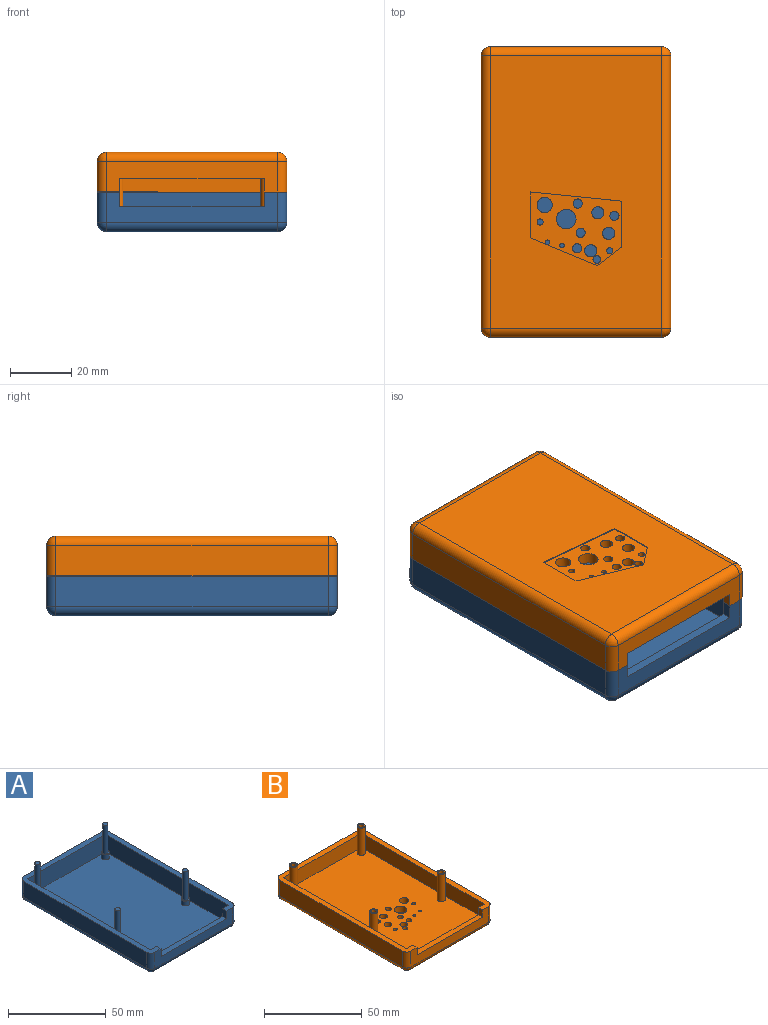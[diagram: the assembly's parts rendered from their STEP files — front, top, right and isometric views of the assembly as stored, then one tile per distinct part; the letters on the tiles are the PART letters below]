
ASSEMBLY  parts=2 mates=1
PART A: 42 faces, bbox 62x95x23 mm
  f0: plane 56x11mm, normal (0,1,0), area 391.6mm2, adj f2,f3,f4,f9,f39,f40,f41
  f1: plane 56x10mm, normal (0,-1,0), area 335.6mm2, adj f2,f32,f36,f38,f39,f40,f41
  f2: plane 95x62mm, normal (0,0,1), area 756.7mm2, adj f0,f1,f3,f6,f7,f8,f9,f10
  f3: plane 89x11mm, normal (1,0,0), area 979mm2, adj f0,f2,f4,f8
  f4: plane 89x56mm, normal (0,0,1), area 4928.6mm2, adj f0,f3,f8,f9,f11,f13,f15,f17
  f5: plane 89x56mm, normal (0,0,-1), area 4984mm2, adj f30,f31,f35,f36
  f6: plane 89x10mm, normal (-1,0,0), area 890mm2, adj f2,f27,f31,f32
  f7: plane 56x10mm, normal (0,1,0), area 560mm2, adj f2,f27,f29,f30
  f8: plane 56x11mm, normal (0,-1,0), area 616mm2, adj f2,f3,f4,f9
  f9: plane 89x11mm, normal (-1,0,0), area 979mm2, adj f0,f2,f4,f8
  f10: plane 89x10mm, normal (1,0,0), area 890mm2, adj f2,f29,f35,f38
  f11: cylinder r=2.1mm len=4.2mm, axis (0,0,-1), area 39.6mm2, adj f4,f12
  f12: plane 4.2x4.2mm, normal (0,0,1), area 7.9mm2, adj f11,f20
  f13: cylinder r=2.1mm len=4.2mm, axis (0,0,-1), area 39.6mm2, adj f4,f14
  f14: plane 4.2x4.2mm, normal (0,0,1), area 7.9mm2, adj f13,f22
  f15: cylinder r=2.1mm len=4.2mm, axis (0,0,-1), area 39.6mm2, adj f4,f16
  f16: plane 4.2x4.2mm, normal (0,0,1), area 7.9mm2, adj f15,f24
  f17: cylinder r=2.1mm len=4.2mm, axis (0,0,-1), area 39.6mm2, adj f4,f18
  f18: plane 4.2x4.2mm, normal (0,0,1), area 7.9mm2, adj f17,f26
  f19: plane 2.75x2.75mm, normal (0,0,1), area 5.9mm2, adj f20
  f20: cylinder r=1.38mm len=18mm, axis (0,0,-1), area 155.5mm2, adj f12,f19
  f21: plane 2.75x2.75mm, normal (0,0,1), area 5.9mm2, adj f22
  f22: cylinder r=1.38mm len=18mm, axis (0,0,-1), area 155.5mm2, adj f14,f21
  f23: plane 2.75x2.75mm, normal (0,0,1), area 5.9mm2, adj f24
  f24: cylinder r=1.38mm len=18mm, axis (0,0,-1), area 155.5mm2, adj f16,f23
  f25: plane 2.75x2.75mm, normal (0,0,1), area 5.9mm2, adj f26
  f26: cylinder r=1.38mm len=18mm, axis (0,0,-1), area 155.5mm2, adj f18,f25
  f27: cylinder r=3mm len=10mm, axis (0,0,-1), area 47.1mm2, adj f2,f6,f7,f28
  f28: sphere r=3mm, area 14.1mm2, adj f27,f30,f31
  f29: cylinder r=3mm len=10mm, axis (0,0,1), area 47.1mm2, adj f2,f7,f10,f33
  f30: cylinder r=3mm len=56mm, axis (-1,0,0), area 263.9mm2, adj f5,f7,f28,f33
  f31: cylinder r=3mm len=89mm, axis (0,-1,0), area 419.4mm2, adj f5,f6,f28,f34
  f32: cylinder r=3mm len=10mm, axis (0,0,1), area 47.1mm2, adj f1,f2,f6,f34
  f33: sphere r=3mm, area 14.1mm2, adj f29,f30,f35
  f34: sphere r=3mm, area 14.1mm2, adj f31,f32,f36
  f35: cylinder r=3mm len=89mm, axis (0,1,0), area 419.4mm2, adj f5,f10,f33,f37
  f36: cylinder r=3mm len=56mm, axis (1,0,0), area 263.9mm2, adj f1,f5,f34,f37
  f37: sphere r=3mm, area 14.1mm2, adj f35,f36,f38
  f38: cylinder r=3mm len=10mm, axis (0,0,-1), area 47.1mm2, adj f1,f2,f10,f37
  f39: plane 4.75x3mm, normal (-1,0,0), area 14.3mm2, adj f0,f1,f2,f41
  f40: plane 4.75x3mm, normal (1,0,0), area 14.3mm2, adj f0,f1,f2,f41
  f41: plane 47.19x3mm, normal (0,0,1), area 141.6mm2, adj f0,f1,f39,f40
PART B: 64 faces, bbox 62x95x21 mm
  f0: plane 95x62mm, normal (0,0,1), area 756.7mm2, adj f32,f33,f34,f35,f36,f37,f38,f39
  f1: cylinder r=2mm len=4mm, axis (0,0,-1), area 46.5mm2, adj f15,f48
  f2: cylinder r=1mm len=3.7mm, axis (0,0,-1), area 23.2mm2, adj f15,f48
  f3: cylinder r=2mm len=4mm, axis (0,0,-1), area 46.5mm2, adj f15,f48
  f4: cylinder r=1.25mm len=3.7mm, axis (0,0,-1), area 29.1mm2, adj f15,f48
  f5: cylinder r=1.5mm len=3.7mm, axis (0,0,-1), area 34.9mm2, adj f15,f48
  f6: cylinder r=0.75mm len=3.7mm, axis (0,0,-1), area 17.4mm2, adj f15,f48
  f7: cylinder r=1.5mm len=3.7mm, axis (0,0,-1), area 34.9mm2, adj f15,f48
  f8: cylinder r=2mm len=4mm, axis (0,0,-1), area 46.5mm2, adj f15,f48
  f9: cylinder r=1.5mm len=3.7mm, axis (0,0,-1), area 34.9mm2, adj f15,f48
  f10: cylinder r=3.19mm len=6.38mm, axis (0,0,-1), area 74.2mm2, adj f15,f48
  f11: cylinder r=0.75mm len=3.7mm, axis (0,0,-1), area 17.4mm2, adj f15,f48
  f12: cylinder r=1mm len=3.7mm, axis (0,0,-1), area 23.2mm2, adj f15,f48
  f13: cylinder r=2.5mm len=5mm, axis (0,0,-1), area 58.1mm2, adj f15,f48
  f14: cylinder r=1.5mm len=3.7mm, axis (0,0,-1), area 34.9mm2, adj f15,f48
  f15: plane 89x56mm, normal (0,0,1), area 4796.2mm2, adj f1,f2,f3,f4,f5,f6,f7,f8
  f16: cylinder r=2.1mm len=17mm, axis (0,0,-1), area 224.3mm2, adj f15,f18
  f17: cylinder r=1.38mm len=17mm, axis (0,0,-1), area 146.9mm2, adj f18,f19
  f18: plane 4.2x4.2mm, normal (0,0,1), area 7.9mm2, adj f16,f17
  f19: plane 2.75x2.75mm, normal (0,0,1), area 5.9mm2, adj f17
  f20: cylinder r=2.1mm len=17mm, axis (0,0,-1), area 224.3mm2, adj f15,f22
  f21: cylinder r=1.38mm len=17mm, axis (0,0,-1), area 146.9mm2, adj f22,f23
  f22: plane 4.2x4.2mm, normal (0,0,1), area 7.9mm2, adj f20,f21
  f23: plane 2.75x2.75mm, normal (0,0,1), area 5.9mm2, adj f21
  f24: cylinder r=1.38mm len=17mm, axis (0,0,-1), area 146.9mm2, adj f26,f27
  f25: cylinder r=2.1mm len=17mm, axis (0,0,-1), area 224.3mm2, adj f15,f26
  f26: plane 4.2x4.2mm, normal (0,0,1), area 7.9mm2, adj f24,f25
  f27: plane 2.75x2.75mm, normal (0,0,1), area 5.9mm2, adj f24
  f28: cylinder r=1.38mm len=17mm, axis (0,0,-1), area 146.9mm2, adj f30,f31
  f29: cylinder r=2.1mm len=17mm, axis (0,0,-1), area 224.3mm2, adj f15,f30
  f30: plane 4.2x4.2mm, normal (0,0,1), area 7.9mm2, adj f28,f29
  f31: plane 2.75x2.75mm, normal (0,0,1), area 5.9mm2, adj f28
  f32: plane 56x9mm, normal (0,-1,0), area 504mm2, adj f0,f15,f33,f35
  f33: plane 89x9mm, normal (1,0,0), area 801mm2, adj f0,f15,f32,f34
  f34: plane 56x9mm, normal (0,1,0), area 291.4mm2, adj f0,f15,f33,f35,f49,f50,f51
  f35: plane 89x9mm, normal (-1,0,0), area 801mm2, adj f0,f15,f32,f34
  f36: plane 56x10mm, normal (0,-1,0), area 347.4mm2, adj f0,f49,f50,f51,f54,f60,f63
  f37: plane 89x10mm, normal (1,0,0), area 890mm2, adj f0,f52,f54,f55
  f38: plane 56x10mm, normal (0,1,0), area 560mm2, adj f0,f52,f56,f57
  f39: plane 89x10mm, normal (-1,0,0), area 890mm2, adj f0,f57,f61,f63
  f40: plane 89x56mm, normal (0,0,-1), area 4430.2mm2, adj f41,f42,f43,f44,f45,f46,f47,f55
  f41: plane 15x0.3mm, normal (1,0,0), area 4.5mm2, adj f40,f42,f47,f48
  f42: plane 30x3mm, normal (0.1,-1,0), area 9mm2, adj f40,f41,f43,f48
  f43: plane 15x0.3mm, normal (-1,0,0), area 4.5mm2, adj f40,f42,f44,f48
  f44: plane 0.3x0.01mm, normal (-0.42,0.91,0), area 0mm2, adj f40,f43,f45,f48
  f45: plane 22.09x9.13mm, normal (-0.38,0.92,0), area 7.2mm2, adj f40,f44,f46,f48
  f46: plane 7.89x6.12mm, normal (0.61,0.79,0), area 3mm2, adj f40,f45,f47,f48
  f47: plane 0.3x0.01mm, normal (0.62,0.78,0), area 0mm2, adj f40,f41,f46,f48
  f48: plane 30x24.13mm, normal (0,0,-1), area 421.5mm2, adj f1,f2,f3,f4,f5,f6,f7,f8
  f49: plane 4.51x3mm, normal (-1,0,0), area 13.5mm2, adj f0,f34,f36,f51
  f50: plane 4.51x3mm, normal (1,0,0), area 13.5mm2, adj f0,f34,f36,f51
  f51: plane 47.19x3mm, normal (0,0,1), area 141.6mm2, adj f34,f36,f49,f50
  f52: cylinder r=3mm len=10mm, axis (0,0,1), area 47.1mm2, adj f0,f37,f38,f53
  f53: sphere r=3mm, area 14.1mm2, adj f52,f55,f56
  f54: cylinder r=3mm len=10mm, axis (0,0,-1), area 47.1mm2, adj f0,f36,f37,f58
  f55: cylinder r=3mm len=89mm, axis (0,1,0), area 419.4mm2, adj f37,f40,f53,f58
  f56: cylinder r=3mm len=56mm, axis (-1,0,0), area 263.9mm2, adj f38,f40,f53,f59
  f57: cylinder r=3mm len=10mm, axis (0,0,1), area 47.1mm2, adj f0,f38,f39,f59
  f58: sphere r=3mm, area 14.1mm2, adj f54,f55,f60
  f59: sphere r=3mm, area 14.1mm2, adj f56,f57,f61
  f60: cylinder r=3mm len=56mm, axis (1,0,0), area 263.9mm2, adj f36,f40,f58,f62
  f61: cylinder r=3mm len=89mm, axis (0,-1,0), area 419.4mm2, adj f39,f40,f59,f62
  f62: sphere r=3mm, area 14.1mm2, adj f60,f61,f63
  f63: cylinder r=3mm len=10mm, axis (0,0,-1), area 47.1mm2, adj f0,f36,f39,f62
PLACE A t=(-90.89,35.61,40.69)mm
PLACE B rot(axis=(0,-1,0),180deg) t=(-31.89,-14.03,66.69)mm
MATE parallel B.f24 <-> A.f17  axis (0,0,-1) through (-35.39,13.47,45.69)mm
